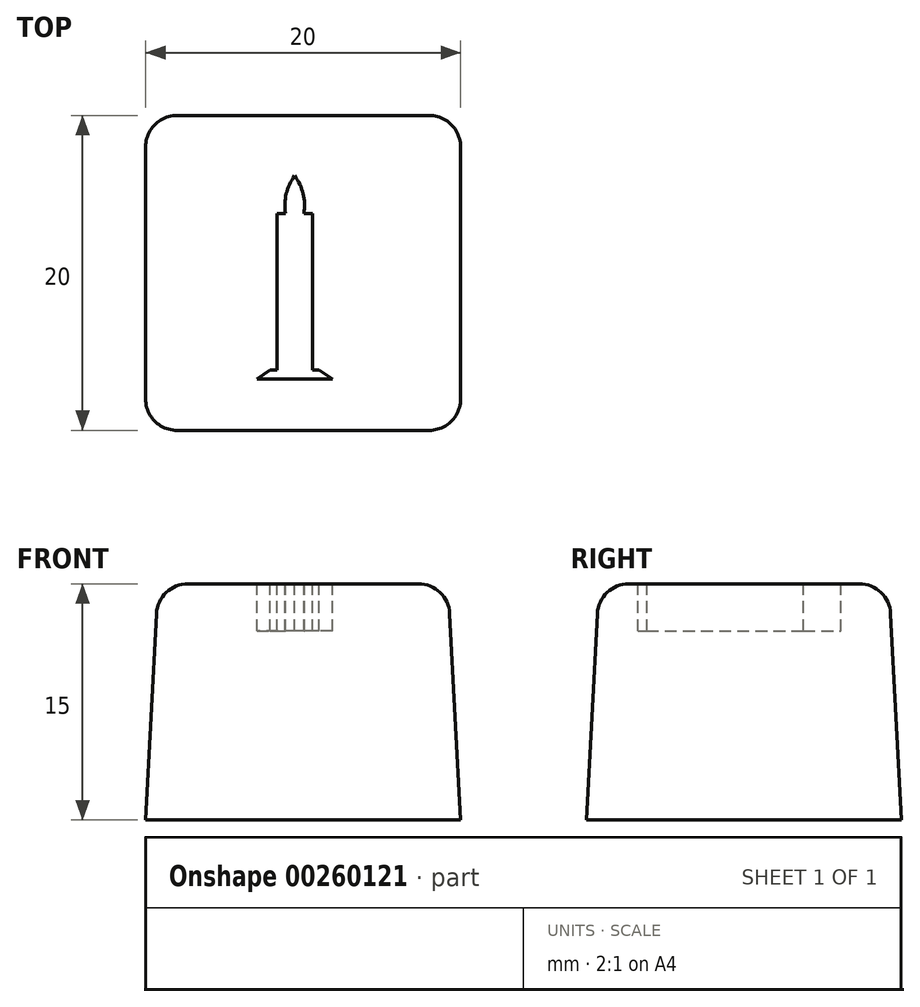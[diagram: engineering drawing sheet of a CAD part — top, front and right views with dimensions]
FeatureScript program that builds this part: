
annotation { "Feature Type Name" : "Feature", "Feature Type Description" : "" }
export const myFeature = defineFeature(function(context is Context, id is Id, definition is map)
    precondition{}
    {
        {
            var Q0;
            Q0=qCreatedBy(makeId("Top.planeOp"),FACE);
            var sketch = newSketch(context, id + "F0", { "sketchPlane" : qUnion([Q0])});
            skLineSegment(sketch, "E0.bottom", {"start": v(-8.64, 12) * mm, "end": v(11.36, 12) * mm});
            skLineSegment(sketch, "E0.top", {"start": v(-8.64, -8) * mm, "end": v(11.36, -8) * mm});
            skLineSegment(sketch, "E0.left", {"start": v(-8.64, 12) * mm, "end": v(-8.64, -8) * mm});
            skLineSegment(sketch, "E0.right", {"start": v(11.36, 12) * mm, "end": v(11.36, -8) * mm});
            skSolve(sketch);
        }
        {
            var Q0;
            Q0 = qSketchRegion(id + "F0", true);
            extrude(context, id + "F1", {"entities" : qUnion([Q0]), "depth" : 15 * mm, "hasDraft" : true, "draftAngle" : 3 * degree, "draftPullDirection" : true});
        }
        {
            var Q0;
            Q0=makeQuery(id+"F1.opExtrude","CAP_EDGE",EDGE,{"disambiguationData":[OSD([sQuery(id+"F0.wireOp",EDGE,"E0.bottom")])],"isStart":false});
            var Q1;
            Q1=makeQuery(id+"F1.opExtrude","SWEPT_EDGE",EDGE,{"disambiguationData":[OSD([sQuery(id+"F0.wireOp",EDGE,"E0.bottom"),sQuery(id+"F0.wireOp",EDGE,"E0.right")])]});
            var Q2;
            Q2=makeQuery(id+"F1.opExtrude","SWEPT_EDGE",EDGE,{"disambiguationData":[OSD([sQuery(id+"F0.wireOp",EDGE,"E0.bottom"),sQuery(id+"F0.wireOp",EDGE,"E0.left")])]});
            var Q3;
            Q3=makeQuery(id+"F1.opExtrude","CAP_EDGE",EDGE,{"disambiguationData":[OSD([sQuery(id+"F0.wireOp",EDGE,"E0.right")])],"isStart":false});
            var Q4;
            Q4=makeQuery(id+"F1.opExtrude","SWEPT_EDGE",EDGE,{"disambiguationData":[OSD([sQuery(id+"F0.wireOp",EDGE,"E0.top"),sQuery(id+"F0.wireOp",EDGE,"E0.right")])]});
            var Q5;
            Q5=makeQuery(id+"F1.opExtrude","SWEPT_EDGE",EDGE,{"disambiguationData":[OSD([sQuery(id+"F0.wireOp",EDGE,"E0.top"),sQuery(id+"F0.wireOp",EDGE,"E0.left")])]});
            var Q6;
            Q6=makeQuery(id+"F1.opExtrude","CAP_EDGE",EDGE,{"disambiguationData":[OSD([sQuery(id+"F0.wireOp",EDGE,"E0.left")])],"isStart":false});
            var Q7;
            Q7=makeQuery(id+"F1.opExtrude","CAP_EDGE",EDGE,{"disambiguationData":[OSD([sQuery(id+"F0.wireOp",EDGE,"E0.top")])],"isStart":false});
            fillet(context, id + "F2", {"entities" : qUnion([Q0, Q1, Q2, Q3, Q4, Q5, Q6, Q7]), "radius" : 2 * mm, "tangentPropagation" : true, "allowEdgeOverflow" : false});
        }
        {
            var Q0;
            Q0=makeQuery(id+"F1.opExtrude","SWEPT_BODY",BODY,{"disambiguationData":[OSD([sQuery(id+"F0.wireOp",EDGE,"E0.bottom"),sQuery(id+"F0.wireOp",EDGE,"E0.top"),sQuery(id+"F0.wireOp",EDGE,"E0.left"),sQuery(id+"F0.wireOp",EDGE,"E0.right")])]});
            deleteBodies(context, id + "F3", {"entities" : qUnion([Q0])});
        }
        {
            var Q0;
            Q0=qCreatedBy(makeId("Top.planeOp"),FACE);
            var sketch = newSketch(context, id + "F4", { "sketchPlane" : qUnion([Q0])});
            skLineSegment(sketch, "E1.bottom", {"start": v(-7.9, 11.28) * mm, "end": v(12.1, 11.28) * mm});
            skLineSegment(sketch, "E1.top", {"start": v(-7.9, -8.72) * mm, "end": v(12.1, -8.72) * mm});
            skLineSegment(sketch, "E1.left", {"start": v(-7.9, 11.28) * mm, "end": v(-7.9, -8.72) * mm});
            skLineSegment(sketch, "E1.right", {"start": v(12.1, 11.28) * mm, "end": v(12.1, -8.72) * mm});
            skSolve(sketch);
        }
        {
            var Q0;
            Q0 = qSketchRegion(id + "F4", true);
            extrude(context, id + "F5", {"entities" : qUnion([Q0]), "depth" : 15 * mm, "hasDraft" : true, "draftAngle" : 3 * degree, "draftPullDirection" : true});
        }
        {
            var Q0;
            Q0=makeQuery(id+"F5.opExtrude","SWEPT_EDGE",EDGE,{"disambiguationData":[OSD([sQuery(id+"F4.wireOp",EDGE,"E1.bottom"),sQuery(id+"F4.wireOp",EDGE,"E1.left")])]});
            var Q1;
            Q1=makeQuery(id+"F5.opExtrude","SWEPT_EDGE",EDGE,{"disambiguationData":[OSD([sQuery(id+"F4.wireOp",EDGE,"E1.bottom"),sQuery(id+"F4.wireOp",EDGE,"E1.right")])]});
            var Q2;
            Q2=makeQuery(id+"F5.opExtrude","SWEPT_EDGE",EDGE,{"disambiguationData":[OSD([sQuery(id+"F4.wireOp",EDGE,"E1.top"),sQuery(id+"F4.wireOp",EDGE,"E1.right")])]});
            var Q3;
            Q3=makeQuery(id+"F5.opExtrude","CAP_EDGE",EDGE,{"disambiguationData":[OSD([sQuery(id+"F4.wireOp",EDGE,"E1.right")])],"isStart":false});
            var Q4;
            Q4=makeQuery(id+"F5.opExtrude","CAP_EDGE",EDGE,{"disambiguationData":[OSD([sQuery(id+"F4.wireOp",EDGE,"E1.bottom")])],"isStart":false});
            var Q5;
            Q5=makeQuery(id+"F5.opExtrude","CAP_EDGE",EDGE,{"disambiguationData":[OSD([sQuery(id+"F4.wireOp",EDGE,"E1.left")])],"isStart":false});
            var Q6;
            Q6=makeQuery(id+"F5.opExtrude","CAP_EDGE",EDGE,{"disambiguationData":[OSD([sQuery(id+"F4.wireOp",EDGE,"E1.top")])],"isStart":false});
            var Q7;
            Q7=makeQuery(id+"F5.opExtrude","SWEPT_EDGE",EDGE,{"disambiguationData":[OSD([sQuery(id+"F4.wireOp",EDGE,"E1.top"),sQuery(id+"F4.wireOp",EDGE,"E1.left")])]});
            fillet(context, id + "F6", {"entities" : qUnion([Q0, Q1, Q2, Q3, Q4, Q5, Q6, Q7]), "radius" : 2 * mm, "tangentPropagation" : true, "allowEdgeOverflow" : false});
        }
        {
            var Q0;
            Q0=makeQuery(id+"F5.opExtrude","CAP_FACE",FACE,{"disambiguationData":[OSD([sQuery(id+"F4.wireOp",EDGE,"E1.bottom"),sQuery(id+"F4.wireOp",EDGE,"E1.top"),sQuery(id+"F4.wireOp",EDGE,"E1.left"),sQuery(id+"F4.wireOp",EDGE,"E1.right")])],"isStart":false});
            var sketch = newSketch(context, id + "F7", { "sketchPlane" : qUnion([Q0])});
            skSolve(sketch);
        }
        {
            var Q0;
            {var subQ0=sQuery(id+"F4.wireOp",EDGE,"E1.right");var subQ1=sQuery(id+"F4.wireOp",EDGE,"E1.left");var subQ2=sQuery(id+"F4.wireOp",EDGE,"E1.top");var subQ3=sQuery(id+"F4.wireOp",EDGE,"E1.bottom");var subQ4=makeQuery(id+"F5.opExtrude","CAP_FACE",FACE,{"disambiguationData":[OSD([subQ3,subQ2,subQ1,subQ0])],"isStart":false});Q0=makeQuery(id+"F7.imprint","IMPRINT",FACE,{"disambiguationData":[TD([[makeQuery(id+"F7.imprint","IMPRINT",EDGE,{"derivedFrom":makeQuery(id+"F6.opFillet","BLEND_EDGE",EDGE,{"blendedFrom":[makeQuery(id+"F5.opExtrude","CAP_EDGE",EDGE,{"disambiguationData":[OSD([subQ3])],"isStart":false}),subQ4],"blendedInto":[subQ4]})}),1.0]])]});}
            var sketch = newSketch(context, id + "F8", { "sketchPlane" : qUnion([Q0])});
            skLineSegment(sketch, "E2", {"start": v(1.56, -5.44) * mm, "end": v(-0.84, -5.44) * mm});
            skLineSegment(sketch, "E3", {"start": v(-0.84, -5.44) * mm, "end": v(0, -4.9) * mm});
            skLineSegment(sketch, "E4", {"start": v(0, -4.9) * mm, "end": v(0.43, -4.9) * mm});
            skLineSegment(sketch, "E5", {"start": v(0.43, -4.9) * mm, "end": v(0.43, 5.05) * mm});
            skLineSegment(sketch, "E6", {"start": v(0.43, 5.05) * mm, "end": v(0.98, 5.05) * mm});
            skArc(sketch, "E7", {"start": v(1.56, 7.45) * mm, "mid": v(1.03, 6.3) * mm, "end": v(0.98, 5.05) * mm});
            skArc(sketch, "E8.MirrorCS", {"start": v(1.56, 7.45) * mm, "mid": v(2.1, 6.3) * mm, "end": v(2.14, 5.05) * mm});
            skLineSegment(sketch, "E9.MirrorCS", {"start": v(2.7, 5.05) * mm, "end": v(2.14, 5.05) * mm});
            skLineSegment(sketch, "E10.MirrorCS", {"start": v(2.7, -4.9) * mm, "end": v(2.7, 5.05) * mm});
            skLineSegment(sketch, "E11.MirrorCS", {"start": v(3.12, -4.9) * mm, "end": v(2.7, -4.9) * mm});
            skLineSegment(sketch, "E12.MirrorCS", {"start": v(3.96, -5.44) * mm, "end": v(3.12, -4.9) * mm});
            skLineSegment(sketch, "E13.MirrorCS", {"start": v(1.56, -5.44) * mm, "end": v(3.96, -5.44) * mm});
            skSolve(sketch);
        }
        {
            var Q0;
            Q0 = qSketchRegion(id + "F8", true);
            extrude(context, id + "F9", {"entities" : qUnion([Q0]), "operationType" : NewBodyOperationType.REMOVE, "oppositeDirection" : true, "depth" : 3 * mm});
        }
    });
